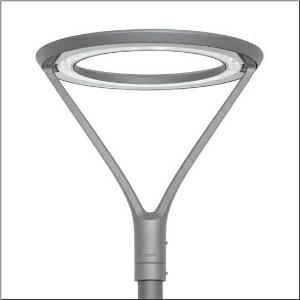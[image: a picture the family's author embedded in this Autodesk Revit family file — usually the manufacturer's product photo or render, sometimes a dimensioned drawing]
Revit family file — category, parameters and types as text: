
# Revit family: dl_r__20___p1_0a_5xa51283nr008_4ff5
name_source: partatom
category: Lighting Fixtures
units: mm (PartAtom-declared; Revit-internal decimal feet)

## family parameters
Cut with Voids When Loaded = No
Host = Face
Light Source = No
Part Type = Normal
Room Calculation Point = No
Round Connector Dimension = Use Diameter
Shared = No

## types (1)
- --- (1 x LED, 3040 lm, 23.2 W, 4000K)
    Apparent Load = 23 VA
    CIE Flux Codes = 31 71 96 100 100
    Color Rendering = 70
    Color Temperature = 4000K
    Default Elevation = 1800 mm
    Description = DL® 20, mast luminaire, primary light control with cycle path optic, highly specular, primary optical cover: cover, of toughened safety glass of clear glass with excellent transmission level, light distribution: P1.0a, light emission: direct distribution, primary light characteristic: asymmetric, installation type: post-top, LED, High Power LED, rated luminous flux: 3.050lm, luminous efficacy: 112lm/W, light colour: 740, colour temperature: 4000K, control gear: Plus, control: overheat protection, power reduction, digital communication interface, constant luminous flux control, time-dependent luminous flux control, flexible luminous flux parameterisation, electronic power reduction, mains connection: 230..240V, 50/60Hz, connection cable pre-assembled, cable length: 5m, start of lifetime: 27W, end of service life: 28W, reduction: 14W, luminaire housing, upper part, of cast aluminium, powder-coated, Siteco® metallic grey (DB 702S), diameter: 690mm, height: 690mm, spigot size: 76mm (post-top), mounting height: 4..6m, luminaire housing, of cast aluminium, powder-coated, Siteco® metallic grey (DB 702S), equipment: standard, protection rating (complete): IP66, insulation class (complete): insulation class II (safety insulation), certification: CE, ENEC, VDE, impact resistance: IK08, permissible operating ambient temperature: -25..+35°C, standard-compliant lighting for roads and squares, packaging unit: 1 piece

Light Distribution: P1.0a
    Height = 690 mm
    Lamp = 1 x LED
    Lamp Light Flux = 3040 lm
    Lamp Power = 23.2 W
    Lamp count = 1
    Length = 690 mm
    Luminous efficacy = 131 lm/W
    Manufacturer = Siteco
    ModVariant = No
    Model = 5XA51283NR008
    Number of Poles = 1
    OnlyDefault = Yes
    Power Factor = 1
    Product Name = DL® 20 | P1.0a
    Product group = mast luminaire | pylon top
    ProductGroupID = 6100
    Protection Class = Protection class II
    Protection Degree = IP 66
    RLX_Detail_Level = 1
    RLX_Emergency_Light_Flux = 0 lm
    RLX_Emergency_Type = 0
    RLX_Emergency_Type_DB = No
    RlxData = <blob elided: 206773 chars, md5=27d3c0f2>
    Socket = socket
    Standby Power = 0 W
    System Light Flux = 3040 lm
    System Power = 23 W
    Type Comments = factory setting: luminous flux: 100 % | dim-lin: 254 | 310 mA
    Type Image = l_1006001.jpg
    URL = http://relux.com
    VarID = @adj_098193
    Voltage = 0 V
    Weight = 0.00 kg
    Width = 0 mm  [stored 0 ft]

note: [stored X ft] marks values corroborated as IEEE doubles in the binary element streams (Revit-internal decimal feet)

## geometry (parser evidence)
native form markers: Blend x4, Sweep x10
no freeform markers — native parametric forms only
